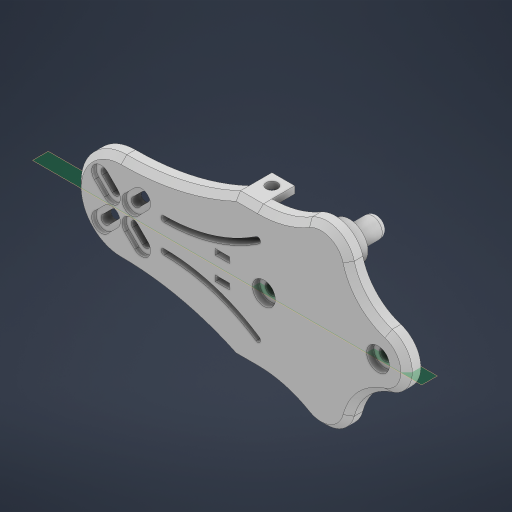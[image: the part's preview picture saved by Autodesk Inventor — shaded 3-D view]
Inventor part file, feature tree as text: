
AUTODESK INVENTOR PART (.ipt)
format: ipt  version: 2024.2 (Build 282272000, 272)  size: 672,256 bytes
history: native  units: in
note: dims shown in document units (in); Inventor stores cm internally (conversion verified against a paired STEP export)
features: extrude x15, sketch x14, projected_geometry x10, mirror x4, fillet x2, plane x1, revolve x1, chamfer x1
ambient origin geometry x8: Origin, YZ Plane, XZ Plane, XY Plane, X Axis, Y Axis, Z Axis, Center Point
bodies: Solid1 (feature_tree)
feature tree (48):
  extrude  "Extrusion1"  Depth=2.3441in
  plane  "Work Plane1"
  extrude  "Extrusion3"  Depth=0.1575in
  mirror  "Mirror1"
  extrude  "Extrusion4"  Depth=0.3677in
  extrude  "Extrusion5"  Depth=0.3937in
  mirror  "Mirror2"
  sketch  "Sketch7"  dims[d18=0.315in d19=0.5906in]
  extrude  "Extrusion6"  Depth=0.5906in
  extrude  "Extrusion7"  TaperAngle=0.0deg  [1 undecoded]
  extrude  "Extrusion8"  Depth=0.0984in
  fillet  "Fillet1"  Radius=0.315in
  extrude  "Extrusion9"  Depth=0.1575in
  mirror  "Mirror3"
  extrude  "Extrusion10"  Depth=0.7874in
  revolve  "Revolution1"  [1 undecoded]
  extrude  "Extrusion11"  Depth=0.1969in TaperAngle=0.0deg
  mirror  "Mirror4"
  extrude  "Extrusion12"  Depth=0.3937in TaperAngle=0.0deg
  fillet  "Fillet2"  Radius=0.0787in
  extrude  "Extrusion14"  Depth=0.6299in
  sketch  "Sketch17"  dims[d45=3.9135in d46=0.1181in d47=0.315in d48=45.0deg d49=0.0974in d50=1.5748in d52=360.0deg d54=0.2362in d55=0.3937in d56=1.378in d57=0.0787in d58=0.0in d59=0.1181in d60=90.0deg d61=0.0787in d62=0.1969in d63=0.2756in d64=0.0in d65=0.0in d66=0.0689in d67=0.0591in d68=0.0in d69=0.315in d70=0.0984in d71=0.0in d72=0.0787in d73=0.0787in d74=0.0787in d75=45.0deg d76=1.1811in d77=0.7874in d78=0.2362in d79=2.3622in d80=1.5748in d81=0.0in d82=0.0in d83=0.7874in d84=0.7874in d85=0.7874in d86=0.7874in d87=0.7874in d88=0.3937in d89=0.0in d90=0.0in d91=0.0in]
  extrude  "Extrusion15"  Depth=0.3937in
  extrude  "Extrusion16"  Depth=0.3937in
  extrude  "Extrusion13"  TaperAngle=45.0deg  [1 undecoded]
  chamfer  "Chamfer1"  Distance=0.0974in
  sketch  "Sketch1"  dims[d3=1.9685in d4=2.3441in]
  sketch  "Sketch4"  dims[d5=0.1969in d6=0.0in d12=0.1575in]
  sketch  "Sketch5"  dims[d13=1.5748in d15=0.3677in]
  projected_geometry  "Projected Loop1"
  sketch  "Sketch6"  dims[d16=0.0787in d17=0.3937in]
  projected_geometry  "Projected Loop2"
  projected_geometry  "Projected Loop3"
  sketch  "Sketch8"  dims[d20=0.1969in d21=0.0in d22=0.0in]
  projected_geometry  "Projected Loop4"
  sketch  "Sketch9"  dims[d23=0.315in d24=0.0984in d25=0.315in d26=0.0in]
  projected_geometry  "Projected Loop5"
  sketch  "Sketch11"  dims[d27=0.1575in d28=0.1575in]
  sketch  "Sketch12"  dims[d29=0.315in d30=0.0in d31=0.7874in]
  projected_geometry  "Projected Loop6"
  sketch  "Sketch13"  dims[d32=0.8268in d33=0.3937in d34=0.0in]
  projected_geometry  "Projected Loop7"
  sketch  "Sketch14"  dims[d35=0.5118in d36=0.1969in d37=0.0in]
  projected_geometry  "Projected Loop8"
  sketch  "Sketch15"  dims[d38=0.2756in d39=0.3937in d40=0.0in d41=0.0787in]
  projected_geometry  "Projected Loop9"
  sketch  "Sketch16"  dims[d42=0.0in d43=0.0in d44=0.6299in]
  projected_geometry  "Projected Loop10"
note: 3 required parameter values undecoded (feature->parameter linkage not recoverable at this tier; creation-order binding heuristic only, values carry confidence <= 0.55)